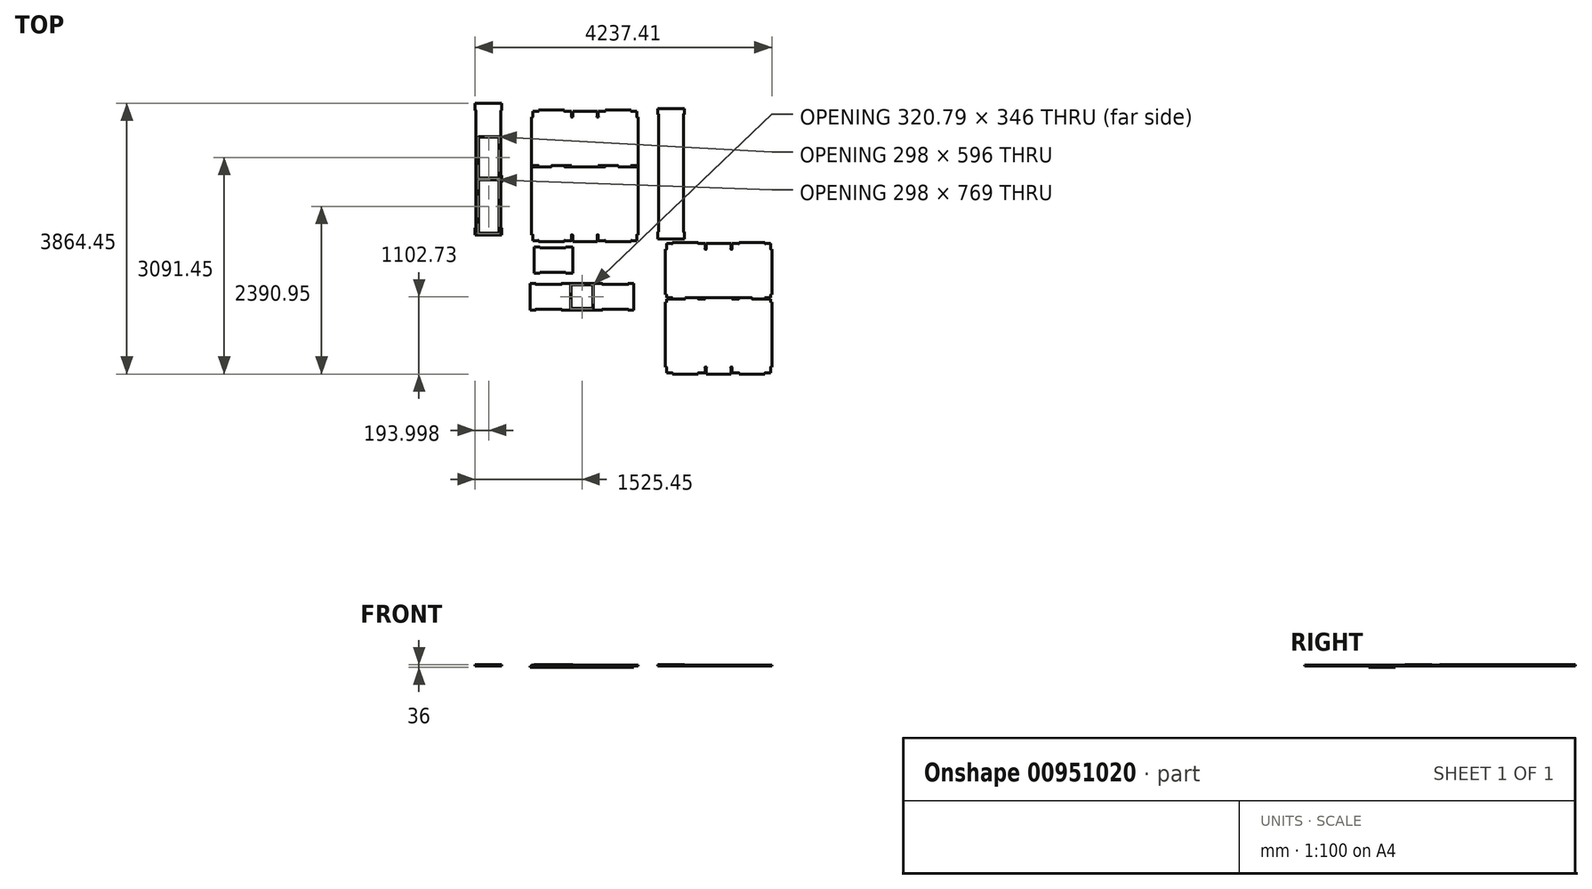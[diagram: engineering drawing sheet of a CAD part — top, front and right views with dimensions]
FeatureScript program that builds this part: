
annotation { "Feature Type Name" : "Feature", "Feature Type Description" : "" }
export const myFeature = defineFeature(function(context is Context, id is Id, definition is map)
    precondition{}
    {
        {
            assignVariable(context, id + "F0", {"name" : "thickness", "anyValue" : 18});
        }
        {
            assignVariable(context, id + "F1", {"name" : "Base", "anyValue" : 12});
        }
        {
            var Q0;
            Q0=qCreatedBy(makeId("Top.planeOp"),FACE);
            var sketch = newSketch(context, id + "F2", { "sketchPlane" : qUnion([Q0])});
            skLineSegment(sketch, "E0.bottom", {"start": v(-1460.53, 1782.83) * mm, "end": v(59.47, 1782.83) * mm});
            skLineSegment(sketch, "E0.top", {"start": v(-1460.53, -97.17) * mm, "end": v(59.47, -97.17) * mm});
            skLineSegment(sketch, "E0.left", {"start": v(-1460.53, 1782.83) * mm, "end": v(-1460.53, -97.17) * mm});
            skLineSegment(sketch, "E0.right", {"start": v(59.47, 1782.83) * mm, "end": v(59.47, -97.17) * mm});
            skLineSegment(sketch, "E1", {"start": v(-700.53, 1782.83) * mm, "end": v(-700.53, -97.17) * mm, "construction": true});
            skLineSegment(sketch, "E2.bottom", {"start": v(-875.53, 1782.83) * mm, "end": v(-893.53, 1782.83) * mm});
            skLineSegment(sketch, "E2.top", {"start": v(-875.53, 1682.83) * mm, "end": v(-893.53, 1682.83) * mm});
            skLineSegment(sketch, "E2.left", {"start": v(-875.53, 1782.83) * mm, "end": v(-875.53, 1682.83) * mm});
            skLineSegment(sketch, "E2.right", {"start": v(-893.53, 1782.83) * mm, "end": v(-893.53, 1682.83) * mm});
            skLineSegment(sketch, "E3.bottom", {"start": v(-875.53, -97.17) * mm, "end": v(-893.53, -97.17) * mm});
            skLineSegment(sketch, "E3.top", {"start": v(-875.53, 2.83) * mm, "end": v(-893.53, 2.83) * mm});
            skLineSegment(sketch, "E3.left", {"start": v(-875.53, -97.17) * mm, "end": v(-875.53, 2.83) * mm});
            skLineSegment(sketch, "E3.right", {"start": v(-893.53, -97.17) * mm, "end": v(-893.53, 2.83) * mm});
            skLineSegment(sketch, "E4.MirrorCS", {"start": v(-507.53, -97.17) * mm, "end": v(-507.53, 2.83) * mm});
            skLineSegment(sketch, "E5.MirrorCS", {"start": v(-525.53, -97.17) * mm, "end": v(-525.53, 2.83) * mm});
            skLineSegment(sketch, "E6.MirrorCS", {"start": v(-525.53, 2.83) * mm, "end": v(-507.53, 2.83) * mm});
            skLineSegment(sketch, "E7.MirrorCS", {"start": v(-525.53, -97.17) * mm, "end": v(-507.53, -97.17) * mm});
            skLineSegment(sketch, "E8.MirrorCS", {"start": v(-525.53, 1782.83) * mm, "end": v(-525.53, 1682.83) * mm});
            skLineSegment(sketch, "E9.MirrorCS", {"start": v(-525.53, 1682.83) * mm, "end": v(-507.53, 1682.83) * mm});
            skLineSegment(sketch, "E10.MirrorCS", {"start": v(-507.53, 1782.83) * mm, "end": v(-507.53, 1682.83) * mm});
            skLineSegment(sketch, "E11.MirrorCS", {"start": v(-525.53, 1782.83) * mm, "end": v(-507.53, 1782.83) * mm});
            skLineSegment(sketch, "E12.bottom", {"start": v(-1460.53, -97.17) * mm, "end": v(-1360.53, -97.17) * mm});
            skLineSegment(sketch, "E12.top", {"start": v(-1460.53, -79.17) * mm, "end": v(-1360.53, -79.17) * mm});
            skLineSegment(sketch, "E12.left", {"start": v(-1460.53, -97.17) * mm, "end": v(-1460.53, -79.17) * mm});
            skLineSegment(sketch, "E12.right", {"start": v(-1360.53, -97.17) * mm, "end": v(-1360.53, -79.17) * mm});
            skLineSegment(sketch, "E13.bottom", {"start": v(-893.53, -97.17) * mm, "end": v(-993.53, -97.17) * mm});
            skLineSegment(sketch, "E13.top", {"start": v(-893.53, -79.17) * mm, "end": v(-993.53, -79.17) * mm});
            skLineSegment(sketch, "E13.left", {"start": v(-893.53, -97.17) * mm, "end": v(-893.53, -79.17) * mm});
            skLineSegment(sketch, "E13.right", {"start": v(-993.53, -97.17) * mm, "end": v(-993.53, -79.17) * mm});
            skLineSegment(sketch, "E14.bottom", {"start": v(-893.53, 1782.83) * mm, "end": v(-993.53, 1782.83) * mm});
            skLineSegment(sketch, "E14.top", {"start": v(-893.53, 1764.83) * mm, "end": v(-993.53, 1764.83) * mm});
            skLineSegment(sketch, "E14.left", {"start": v(-893.53, 1782.83) * mm, "end": v(-893.53, 1764.83) * mm});
            skLineSegment(sketch, "E14.right", {"start": v(-993.53, 1782.83) * mm, "end": v(-993.53, 1764.83) * mm});
            skLineSegment(sketch, "E15.bottom", {"start": v(-1460.53, 1782.83) * mm, "end": v(-1360.53, 1782.83) * mm});
            skLineSegment(sketch, "E15.top", {"start": v(-1460.53, 1764.83) * mm, "end": v(-1360.53, 1764.83) * mm});
            skLineSegment(sketch, "E15.left", {"start": v(-1460.53, 1782.83) * mm, "end": v(-1460.53, 1764.83) * mm});
            skLineSegment(sketch, "E15.right", {"start": v(-1360.53, 1782.83) * mm, "end": v(-1360.53, 1764.83) * mm});
            skLineSegment(sketch, "E16.MirrorCS", {"start": v(-507.53, 1764.83) * mm, "end": v(-407.53, 1764.83) * mm});
            skLineSegment(sketch, "E17.MirrorCS", {"start": v(-407.53, 1782.83) * mm, "end": v(-407.53, 1764.83) * mm});
            skLineSegment(sketch, "E18.MirrorCS", {"start": v(59.47, 1764.83) * mm, "end": v(-40.53, 1764.83) * mm});
            skLineSegment(sketch, "E19.MirrorCS", {"start": v(-40.53, 1782.83) * mm, "end": v(-40.53, 1764.83) * mm});
            skLineSegment(sketch, "E20.MirrorCS", {"start": v(-507.53, -79.17) * mm, "end": v(-407.53, -79.17) * mm});
            skLineSegment(sketch, "E21.MirrorCS", {"start": v(-407.53, -97.17) * mm, "end": v(-407.53, -79.17) * mm});
            skLineSegment(sketch, "E22.MirrorCS", {"start": v(59.47, -79.17) * mm, "end": v(-40.53, -79.17) * mm});
            skLineSegment(sketch, "E23.MirrorCS", {"start": v(-40.53, -97.17) * mm, "end": v(-40.53, -79.17) * mm});
            skLineSegment(sketch, "E24.bottom", {"start": v(-1460.53, 1764.83) * mm, "end": v(-1442.53, 1764.83) * mm});
            skLineSegment(sketch, "E24.top", {"start": v(-1460.53, 1682.83) * mm, "end": v(-1442.53, 1682.83) * mm});
            skLineSegment(sketch, "E24.left", {"start": v(-1460.53, 1764.83) * mm, "end": v(-1460.53, 1682.83) * mm});
            skLineSegment(sketch, "E24.right", {"start": v(-1442.53, 1764.83) * mm, "end": v(-1442.53, 1682.83) * mm});
            skLineSegment(sketch, "E25.bottom", {"start": v(-1460.53, -79.17) * mm, "end": v(-1442.53, -79.17) * mm});
            skLineSegment(sketch, "E25.top", {"start": v(-1460.53, 2.83) * mm, "end": v(-1442.53, 2.83) * mm});
            skLineSegment(sketch, "E25.left", {"start": v(-1460.53, -79.17) * mm, "end": v(-1460.53, 2.83) * mm});
            skLineSegment(sketch, "E25.right", {"start": v(-1442.53, -79.17) * mm, "end": v(-1442.53, 2.83) * mm});
            skLineSegment(sketch, "E26.MirrorCS", {"start": v(59.47, 2.83) * mm, "end": v(41.47, 2.83) * mm});
            skLineSegment(sketch, "E27.MirrorCS", {"start": v(41.47, -79.17) * mm, "end": v(41.47, 2.83) * mm});
            skLineSegment(sketch, "E28.MirrorCS", {"start": v(59.47, 1682.83) * mm, "end": v(41.47, 1682.83) * mm});
            skLineSegment(sketch, "E29.MirrorCS", {"start": v(41.47, 1764.83) * mm, "end": v(41.47, 1682.83) * mm});
            skLineSegment(sketch, "E30", {"start": v(-1460.53, 982.83) * mm, "end": v(59.47, 982.83) * mm, "construction": true});
            skLineSegment(sketch, "E31", {"start": v(59.47, 982.83) * mm, "end": v(-930.26, 982.83) * mm, "construction": true});
            skLineSegment(sketch, "E32.bottom", {"start": v(-1460.53, 991.83) * mm, "end": v(-1360.53, 991.83) * mm});
            skLineSegment(sketch, "E32.top", {"start": v(-1442.53, 973.83) * mm, "end": v(-1360.53, 973.83) * mm});
            skLineSegment(sketch, "E32.left", {"start": v(-1460.53, 991.83) * mm, "end": v(-1460.53, 973.83) * mm});
            skLineSegment(sketch, "E32.right", {"start": v(-1360.53, 991.83) * mm, "end": v(-1360.53, 973.83) * mm});
            skLineSegment(sketch, "E33.bottom", {"start": v(-993.53, 991.83) * mm, "end": v(-893.53, 991.83) * mm});
            skLineSegment(sketch, "E33.top", {"start": v(-993.53, 973.83) * mm, "end": v(-893.53, 973.83) * mm});
            skLineSegment(sketch, "E33.left", {"start": v(-993.53, 991.83) * mm, "end": v(-993.53, 973.83) * mm});
            skLineSegment(sketch, "E33.right", {"start": v(-893.53, 991.83) * mm, "end": v(-893.53, 973.83) * mm});
            skLineSegment(sketch, "E34.MirrorCS", {"start": v(41.47, 973.83) * mm, "end": v(-40.53, 973.83) * mm});
            skLineSegment(sketch, "E35.MirrorCS", {"start": v(59.47, 991.83) * mm, "end": v(-40.53, 991.83) * mm});
            skLineSegment(sketch, "E36.MirrorCS", {"start": v(-40.53, 991.83) * mm, "end": v(-40.53, 973.83) * mm});
            skLineSegment(sketch, "E37.MirrorCS", {"start": v(-407.53, 973.83) * mm, "end": v(-507.53, 973.83) * mm});
            skLineSegment(sketch, "E38.MirrorCS", {"start": v(-407.53, 991.83) * mm, "end": v(-407.53, 973.83) * mm});
            skLineSegment(sketch, "E39.MirrorCS", {"start": v(-407.53, 991.83) * mm, "end": v(-507.53, 991.83) * mm});
            skLineSegment(sketch, "E40.MirrorCS", {"start": v(-507.53, 991.83) * mm, "end": v(-507.53, 973.83) * mm});
            skLineSegment(sketch, "E41.bottom", {"start": v(-1177.03, 991.83) * mm, "end": v(-993.53, 991.83) * mm});
            skLineSegment(sketch, "E41.top", {"start": v(-1360.53, 973.83) * mm, "end": v(-1177.03, 973.83) * mm});
            skLineSegment(sketch, "E42", {"start": v(-1177.03, 991.83) * mm, "end": v(-1177.03, 973.83) * mm});
            skLineSegment(sketch, "E43", {"start": v(-893.53, 973.83) * mm, "end": v(-507.53, 973.83) * mm});
            skLineSegment(sketch, "E44.bottom", {"start": v(-407.53, 991.83) * mm, "end": v(-224.03, 991.83) * mm});
            skLineSegment(sketch, "E44.top", {"start": v(-224.03, 973.83) * mm, "end": v(-40.53, 973.83) * mm});
            skLineSegment(sketch, "E45", {"start": v(-224.03, 991.83) * mm, "end": v(-224.03, 973.83) * mm});
            skLineSegment(sketch, "E46.bottom", {"start": v(-1460.53, 991.83) * mm, "end": v(-1442.53, 991.83) * mm});
            skLineSegment(sketch, "E46.left", {"start": v(-1460.53, 993.83) * mm, "end": v(-1460.53, 991.83) * mm});
            skLineSegment(sketch, "E46.right", {"start": v(-1442.53, 991.83) * mm, "end": v(-1442.53, 973.83) * mm});
            skLineSegment(sketch, "E47.bottom", {"start": v(59.47, 991.83) * mm, "end": v(41.47, 991.83) * mm});
            skLineSegment(sketch, "E47.left", {"start": v(59.47, 993.83) * mm, "end": v(59.47, 991.83) * mm});
            skLineSegment(sketch, "E47.right", {"start": v(41.47, 991.83) * mm, "end": v(41.47, 973.83) * mm});
            skPoint(sketch, "E48.orphan", {"position": v(59.47, 973.83) * mm});
            skLineSegment(sketch, "E49.bottom", {"start": v(-893.53, 1782.83) * mm, "end": v(-507.53, 1782.83) * mm});
            skLineSegment(sketch, "E49.top", {"start": v(-893.53, 1764.83) * mm, "end": v(-507.53, 1764.83) * mm});
            skLineSegment(sketch, "E49.right", {"start": v(-507.53, 1782.83) * mm, "end": v(-507.53, 1764.83) * mm});
            skCircle(sketch, "E50", {"center": v(-1445.35, 1685.66) * mm, "radius": 4 * mm});
            skLineSegment(sketch, "E51", {"start": v(-1442.53, 1682.83) * mm, "end": v(-1445.35, 1685.66) * mm});
            skCircle(sketch, "E52", {"center": v(-1363.15, 1767.84) * mm, "radius": 4 * mm});
            skLineSegment(sketch, "E53", {"start": v(-1360.53, 1764.83) * mm, "end": v(-1363.15, 1767.84) * mm});
            skCircle(sketch, "E54", {"center": v(-990.7, 1767.66) * mm, "radius": 4 * mm});
            skLineSegment(sketch, "E55", {"start": v(-993.53, 1764.83) * mm, "end": v(-990.7, 1767.66) * mm});
            skCircle(sketch, "E56", {"center": v(-890.7, 1685.66) * mm, "radius": 4 * mm});
            skLineSegment(sketch, "E57", {"start": v(-893.53, 1682.83) * mm, "end": v(-890.7, 1685.66) * mm});
            skCircle(sketch, "E58", {"center": v(-878.35, 1685.66) * mm, "radius": 4 * mm});
            skLineSegment(sketch, "E59", {"start": v(-875.53, 1682.83) * mm, "end": v(-878.35, 1685.66) * mm});
            skCircle(sketch, "E60", {"center": v(-1439.7, 976.66) * mm, "radius": 4 * mm});
            skCircle(sketch, "E61", {"center": v(-1363.35, 989) * mm, "radius": 4 * mm});
            skLineSegment(sketch, "E62", {"start": v(-1360.53, 991.83) * mm, "end": v(-1363.35, 989) * mm});
            skLineSegment(sketch, "E63", {"start": v(-1442.53, 973.83) * mm, "end": v(-1439.7, 976.66) * mm});
            skArc(sketch, "E64", {"start": v(-1171.37, 991.83) * mm, "mid": v(-1177.03, 991.83) * mm, "end": v(-1177.03, 986.17) * mm});
            skLineSegment(sketch, "E65", {"start": v(-1177.03, 991.83) * mm, "end": v(-1174.2, 989) * mm});
            skArc(sketch, "E66", {"start": v(-1182.68, 973.83) * mm, "mid": v(-1177.03, 973.83) * mm, "end": v(-1177.03, 979.49) * mm});
            skLineSegment(sketch, "E67", {"start": v(-1177.03, 973.83) * mm, "end": v(-1179.85, 976.66) * mm});
            skCircle(sketch, "E68", {"center": v(-990.7, 976.66) * mm, "radius": 4 * mm});
            skLineSegment(sketch, "E69", {"start": v(-993.53, 973.83) * mm, "end": v(-990.7, 976.66) * mm});
            skCircle(sketch, "E70", {"center": v(-896.35, 989) * mm, "radius": 4 * mm});
            skLineSegment(sketch, "E71", {"start": v(-893.53, 991.83) * mm, "end": v(-896.35, 989) * mm});
            skCircle(sketch, "E72", {"center": v(-1445.35, 0) * mm, "radius": 4 * mm});
            skLineSegment(sketch, "E73", {"start": v(-1442.53, 2.83) * mm, "end": v(-1445.35, 0) * mm});
            skCircle(sketch, "E74", {"center": v(-1363.35, -82) * mm, "radius": 4 * mm});
            skLineSegment(sketch, "E75", {"start": v(-1360.53, -79.17) * mm, "end": v(-1363.35, -82) * mm});
            skCircle(sketch, "E76", {"center": v(-990.7, -82) * mm, "radius": 4 * mm});
            skLineSegment(sketch, "E77", {"start": v(-993.53, -79.17) * mm, "end": v(-990.7, -82) * mm});
            skCircle(sketch, "E78", {"center": v(-890.7, 0) * mm, "radius": 4 * mm});
            skCircle(sketch, "E79", {"center": v(-878.35, 0) * mm, "radius": 4 * mm});
            skLineSegment(sketch, "E80", {"start": v(-875.53, 2.83) * mm, "end": v(-878.35, 0) * mm});
            skLineSegment(sketch, "E81", {"start": v(-893.53, 2.83) * mm, "end": v(-890.7, 0) * mm});
            skCircle(sketch, "E82.MirrorC", {"center": v(-522.7, 0) * mm, "radius": 4 * mm});
            skCircle(sketch, "E83.MirrorC", {"center": v(-510.35, 0) * mm, "radius": 4 * mm});
            skCircle(sketch, "E84.MirrorC", {"center": v(-410.35, -82) * mm, "radius": 4 * mm});
            skCircle(sketch, "E85.MirrorC", {"center": v(-37.7, -82) * mm, "radius": 4 * mm});
            skCircle(sketch, "E86.MirrorC", {"center": v(44.3, 0) * mm, "radius": 4 * mm});
            skCircle(sketch, "E87.MirrorC", {"center": v(38.65, 976.66) * mm, "radius": 4 * mm});
            skCircle(sketch, "E88.MirrorC", {"center": v(-37.7, 989) * mm, "radius": 4 * mm});
            skArc(sketch, "E89.MirrorCS", {"start": v(-218.37, 973.83) * mm, "mid": v(-224.03, 973.83) * mm, "end": v(-224.03, 979.49) * mm});
            skArc(sketch, "E90.MirrorCS", {"start": v(-229.68, 991.83) * mm, "mid": v(-224.03, 991.83) * mm, "end": v(-224.03, 986.17) * mm});
            skCircle(sketch, "E91.MirrorC", {"center": v(-410.35, 976.66) * mm, "radius": 4 * mm});
            skCircle(sketch, "E92.MirrorC", {"center": v(-504.7, 989) * mm, "radius": 4 * mm});
            skCircle(sketch, "E93.MirrorC", {"center": v(44.3, 1685.66) * mm, "radius": 4 * mm});
            skCircle(sketch, "E94.MirrorC", {"center": v(-37.9, 1767.84) * mm, "radius": 4 * mm});
            skCircle(sketch, "E95.MirrorC", {"center": v(-410.35, 1767.66) * mm, "radius": 4 * mm});
            skCircle(sketch, "E96.MirrorC", {"center": v(-510.35, 1685.66) * mm, "radius": 4 * mm});
            skCircle(sketch, "E97.MirrorC", {"center": v(-522.7, 1685.66) * mm, "radius": 4 * mm});
            skSolve(sketch);
        }
        {
            var Q0;
            {var subQ23=sQuery(id+"F2.wireOp",EDGE,"E43");Q0=makeQuery(id+"F2.imprint","IMPRINT",FACE,{"disambiguationData":[TD([[makeQuery(id+"F2.imprint","IMPRINT",EDGE,{"derivedFrom":subQ23}),1.0]])]});}
            extrude(context, id + "F3", {"entities" : qUnion([Q0]), "depth" : getVariable(context, 'Base') * mm, "offsetDistance" : 25 * mm});
        }
        {
            var Q0;
            Q0=qCreatedBy(makeId("Top.planeOp"),FACE);
            var sketch = newSketch(context, id + "F4", { "sketchPlane" : qUnion([Q0])});
            skLineSegment(sketch, "E98.bottom", {"start": v(719.43, 1805.64) * mm, "end": v(719.43, 1805.64) * mm});
            skLineSegment(sketch, "E98.top", {"start": v(719.43, -56.36) * mm, "end": v(719.43, -56.36) * mm});
            skLineSegment(sketch, "E98.left", {"start": v(719.43, 1805.64) * mm, "end": v(719.43, 1723.64) * mm});
            skLineSegment(sketch, "E98.right", {"start": v(719.43, 1805.64) * mm, "end": v(719.43, -56.36) * mm});
            skLineSegment(sketch, "E99.bottom", {"start": v(719.43, 1805.64) * mm, "end": v(339.43, 1805.64) * mm});
            skLineSegment(sketch, "E99.top", {"start": v(719.43, -56.36) * mm, "end": v(339.43, -56.36) * mm});
            skLineSegment(sketch, "E99.right", {"start": v(339.43, 1805.64) * mm, "end": v(339.43, -56.36) * mm});
            skLineSegment(sketch, "E100.bottom", {"start": v(339.43, 1805.64) * mm, "end": v(719.43, 1805.64) * mm});
            skLineSegment(sketch, "E100.top", {"start": v(339.43, 1723.64) * mm, "end": v(719.43, 1723.64) * mm});
            skLineSegment(sketch, "E100.right", {"start": v(339.43, 1805.64) * mm, "end": v(339.43, 1723.64) * mm});
            skLineSegment(sketch, "E101.top", {"start": v(719.43, 43.64) * mm, "end": v(339.43, 43.64) * mm});
            skLineSegment(sketch, "E101.left", {"start": v(339.43, -56.36) * mm, "end": v(339.43, 43.64) * mm});
            skLineSegment(sketch, "E101.right", {"start": v(719.43, -56.36) * mm, "end": v(719.43, 43.64) * mm});
            skLineSegment(sketch, "E102.trimOffspring", {"start": v(719.43, 43.64) * mm, "end": v(719.43, -56.36) * mm});
            skLineSegment(sketch, "E103.bottom", {"start": v(719.43, 1723.64) * mm, "end": v(707.43, 1723.64) * mm});
            skLineSegment(sketch, "E103.top", {"start": v(719.43, 43.64) * mm, "end": v(707.43, 43.64) * mm});
            skLineSegment(sketch, "E103.left", {"start": v(719.43, 1723.64) * mm, "end": v(719.43, 43.64) * mm});
            skLineSegment(sketch, "E103.right", {"start": v(707.43, 1723.64) * mm, "end": v(707.43, 43.64) * mm});
            skLineSegment(sketch, "E104.bottom", {"start": v(339.43, 43.64) * mm, "end": v(352.43, 43.64) * mm});
            skLineSegment(sketch, "E104.top", {"start": v(339.43, 1723.64) * mm, "end": v(352.43, 1723.64) * mm});
            skLineSegment(sketch, "E104.left", {"start": v(339.43, 43.64) * mm, "end": v(339.43, 1723.64) * mm});
            skLineSegment(sketch, "E104.right", {"start": v(352.43, 43.64) * mm, "end": v(352.43, 1723.64) * mm});
            skCircle(sketch, "E105", {"center": v(349.6, 46.47) * mm, "radius": 4 * mm});
            skLineSegment(sketch, "E106", {"start": v(352.43, 43.64) * mm, "end": v(349.6, 46.47) * mm});
            skCircle(sketch, "E107", {"center": v(710.26, 46.47) * mm, "radius": 4 * mm});
            skLineSegment(sketch, "E108", {"start": v(707.43, 43.64) * mm, "end": v(710.26, 46.47) * mm});
            skCircle(sketch, "E109", {"center": v(349.6, 1720.82) * mm, "radius": 4 * mm});
            skLineSegment(sketch, "E110", {"start": v(352.43, 1723.64) * mm, "end": v(349.6, 1720.82) * mm});
            skCircle(sketch, "E111", {"center": v(710.26, 1720.82) * mm, "radius": 4 * mm});
            skLineSegment(sketch, "E112", {"start": v(707.43, 1723.64) * mm, "end": v(710.26, 1720.82) * mm});
            skSolve(sketch);
        }
        {
            var Q0;
            {var subQ9=sQuery(id+"F4.wireOp",EDGE,"E98.left");Q0=makeQuery(id+"F4.imprint","IMPRINT",FACE,{"disambiguationData":[TD([[makeQuery(id+"F4.imprint","IMPRINT",EDGE,{"derivedFrom":subQ9}),-1.0]])]});}
            var Q1;
            {var subQ7=sQuery(id+"F4.wireOp",EDGE,"E111");var subQ8=sQuery(id+"F4.wireOp",EDGE,"E103.right");var subQ9=makeQuery(id+"F4.imprint","INTERSECT",VERTEX,{"derivedFrom":[subQ8,subQ7]});Q1=makeQuery(id+"F4.imprint","IMPRINT",FACE,{"disambiguationData":[TD([[makeQuery(id+"F4.imprint","IMPRINT",EDGE,{"disambiguationData":[TD([[subQ9,-1.0]])],"derivedFrom":subQ8}),-1.0]])]});}
            var Q2;
            {var subQ5=sQuery(id+"F4.wireOp",EDGE,"E99.top");Q2=makeQuery(id+"F4.imprint","IMPRINT",FACE,{"disambiguationData":[TD([[makeQuery(id+"F4.imprint","IMPRINT",EDGE,{"derivedFrom":subQ5}),-1.0]])]});}
            extrude(context, id + "F5", {"entities" : qUnion([Q0, Q1, Q2]), "depth" : (getVariable(context, 'thickness')) * mm, "offsetDistance" : 25 * mm});
        }
        {
            var Q0;
            Q0=qCreatedBy(makeId("Top.planeOp"),FACE);
            var sketch = newSketch(context, id + "F6", { "sketchPlane" : qUnion([Q0])});
            skLineSegment(sketch, "E113.bottom", {"start": v(-1440.4, -167.9) * mm, "end": v(-873.9, -167.9) * mm});
            skLineSegment(sketch, "E113.top", {"start": v(-1440.4, -547.9) * mm, "end": v(-873.9, -547.9) * mm});
            skLineSegment(sketch, "E113.left", {"start": v(-1440.4, -167.9) * mm, "end": v(-1440.4, -547.9) * mm});
            skLineSegment(sketch, "E113.right", {"start": v(-873.9, -167.9) * mm, "end": v(-873.9, -547.9) * mm});
            skLineSegment(sketch, "E114.bottom", {"start": v(-873.9, -547.9) * mm, "end": v(-1440.4, -547.9) * mm});
            skLineSegment(sketch, "E114.top", {"start": v(-973.9, -180.9) * mm, "end": v(-1340.4, -180.9) * mm});
            skLineSegment(sketch, "E114.left", {"start": v(-873.9, -547.9) * mm, "end": v(-873.9, -180.9) * mm});
            skLineSegment(sketch, "E114.right", {"start": v(-1440.4, -547.9) * mm, "end": v(-1440.4, -180.9) * mm});
            skLineSegment(sketch, "E115.bottom", {"start": v(-1340.4, -167.9) * mm, "end": v(-973.9, -167.9) * mm});
            skLineSegment(sketch, "E115.top", {"start": v(-1340.4, -180.9) * mm, "end": v(-973.9, -180.9) * mm});
            skLineSegment(sketch, "E115.left", {"start": v(-1340.4, -167.9) * mm, "end": v(-1340.4, -180.9) * mm});
            skLineSegment(sketch, "E115.right", {"start": v(-973.9, -167.9) * mm, "end": v(-973.9, -180.9) * mm});
            skLineSegment(sketch, "E116.bottom", {"start": v(-1340.4, -547.9) * mm, "end": v(-973.9, -547.9) * mm});
            skLineSegment(sketch, "E116.top", {"start": v(-1340.4, -535.9) * mm, "end": v(-973.9, -535.9) * mm});
            skLineSegment(sketch, "E116.left", {"start": v(-1340.4, -547.9) * mm, "end": v(-1340.4, -535.9) * mm});
            skLineSegment(sketch, "E116.right", {"start": v(-973.9, -547.9) * mm, "end": v(-973.9, -535.9) * mm});
            skLineSegment(sketch, "E117.bottom", {"start": v(-1440.4, -167.9) * mm, "end": v(-1422.4, -167.9) * mm});
            skLineSegment(sketch, "E117.top", {"start": v(-1440.4, -547.9) * mm, "end": v(-1422.4, -547.9) * mm});
            skLineSegment(sketch, "E117.right", {"start": v(-1422.4, -167.9) * mm, "end": v(-1422.4, -547.9) * mm});
            skLineSegment(sketch, "E118.trimOffspring", {"start": v(-1422.4, -180.9) * mm, "end": v(-1440.4, -180.9) * mm});
            skCircle(sketch, "E119", {"center": v(-1337.57, -178.07) * mm, "radius": 4 * mm});
            skLineSegment(sketch, "E120", {"start": v(-1340.4, -180.9) * mm, "end": v(-1337.57, -178.07) * mm});
            skCircle(sketch, "E121", {"center": v(-976.72, -178.07) * mm, "radius": 4 * mm});
            skLineSegment(sketch, "E122", {"start": v(-973.9, -180.9) * mm, "end": v(-976.72, -178.07) * mm});
            skCircle(sketch, "E123", {"center": v(-1337.57, -538.73) * mm, "radius": 4 * mm});
            skLineSegment(sketch, "E124", {"start": v(-1340.4, -535.9) * mm, "end": v(-1337.57, -538.73) * mm});
            skCircle(sketch, "E125", {"center": v(-976.72, -538.73) * mm, "radius": 4 * mm});
            skLineSegment(sketch, "E126", {"start": v(-973.9, -535.9) * mm, "end": v(-976.72, -538.73) * mm});
            skSolve(sketch);
        }
        {
            var Q0;
            {var subQ12=sQuery(id+"F6.wireOp",EDGE,"E113.right");var subQ13=makeQuery(id+"F6.imprint","IMPRINT",VERTEX,{"derivedFrom":subQ12});Q0=makeQuery(id+"F6.imprint","IMPRINT",FACE,{"disambiguationData":[TD([[makeQuery(id+"F6.imprint","IMPRINT",EDGE,{"disambiguationData":[TD([[subQ13,-1.0]])],"derivedFrom":subQ12}),-1.0]])]});}
            extrude(context, id + "F7", {"entities" : qUnion([Q0]), "depth" : (getVariable(context, 'thickness')) * mm, "offsetDistance" : 25 * mm});
        }
        {
            var Q0;
            Q0=qCreatedBy(makeId("Top.planeOp"),FACE);
            var sketch = newSketch(context, id + "F8", { "sketchPlane" : qUnion([Q0])});
            skLineSegment(sketch, "E127.bottom", {"start": v(-1887.45, 1880) * mm, "end": v(-2267.45, 1880) * mm});
            skLineSegment(sketch, "E127.top", {"start": v(-1887.45, 0) * mm, "end": v(-2267.45, 0) * mm});
            skLineSegment(sketch, "E127.right", {"start": v(-2267.45, 1880) * mm, "end": v(-2267.45, 0) * mm});
            skLineSegment(sketch, "E128", {"start": v(-2179.45, 1480) * mm, "end": v(-1916.45, 1480) * mm, "construction": true});
            skLineSegment(sketch, "E129", {"start": v(-2179.45, 800) * mm, "end": v(-1916.45, 800) * mm, "construction": true});
            skLineSegment(sketch, "E130.bottom", {"start": v(-2212.45, 1405) * mm, "end": v(-1934.45, 1405) * mm});
            skLineSegment(sketch, "E130.top", {"start": v(-2212.45, 809) * mm, "end": v(-1934.45, 809) * mm});
            skLineSegment(sketch, "E130.left", {"start": v(-2222.45, 1395) * mm, "end": v(-2222.45, 819) * mm});
            skLineSegment(sketch, "E130.right", {"start": v(-1924.45, 1395) * mm, "end": v(-1924.45, 819) * mm});
            skLineSegment(sketch, "E131.top", {"start": v(-2212.45, 791) * mm, "end": v(-1934.45, 791) * mm});
            skLineSegment(sketch, "E131.left", {"start": v(-2222.45, 32) * mm, "end": v(-2222.45, 781) * mm});
            skLineSegment(sketch, "E131.right", {"start": v(-1924.45, 32) * mm, "end": v(-1924.45, 781) * mm});
            skPoint(sketch, "E132.visualSharp", {"position": v(-2222.45, 809) * mm});
            skPoint(sketch, "E133.visualSharp", {"position": v(-1924.45, 809) * mm});
            skPoint(sketch, "E134.visualSharp", {"position": v(-1924.45, 1405) * mm});
            skPoint(sketch, "E135.visualSharp", {"position": v(-2222.45, 1405) * mm});
            skPoint(sketch, "E136.visualSharp", {"position": v(-2222.45, 791) * mm});
            skPoint(sketch, "E137.visualSharp", {"position": v(-1924.45, 791) * mm});
            skPoint(sketch, "E138.visualSharp", {"position": v(-2222.45, 22) * mm});
            skPoint(sketch, "E139.visualSharp", {"position": v(-1924.45, 22) * mm});
            skLineSegment(sketch, "E140.bottom", {"start": v(-2267.45, 1780) * mm, "end": v(-2255.45, 1780) * mm});
            skLineSegment(sketch, "E140.top", {"start": v(-2267.45, 100) * mm, "end": v(-2255.45, 100) * mm});
            skLineSegment(sketch, "E140.left", {"start": v(-2267.45, 1780) * mm, "end": v(-2267.45, 100) * mm});
            skLineSegment(sketch, "E140.right", {"start": v(-2255.45, 1780) * mm, "end": v(-2255.45, 100) * mm});
            skLineSegment(sketch, "E141", {"start": v(-2212.45, 22) * mm, "end": v(-1934.45, 22) * mm});
            skLineSegment(sketch, "E142", {"start": v(-1887.45, 0) * mm, "end": v(-1887.45, 1880) * mm});
            skLineSegment(sketch, "E143.bottom", {"start": v(-1887.45, 0) * mm, "end": v(-1900.45, 0) * mm});
            skLineSegment(sketch, "E143.top", {"start": v(-1887.45, 100) * mm, "end": v(-1900.45, 100) * mm});
            skLineSegment(sketch, "E143.left", {"start": v(-1887.45, 0) * mm, "end": v(-1887.45, 100) * mm});
            skLineSegment(sketch, "E143.right", {"start": v(-1900.45, 0) * mm, "end": v(-1900.45, 100) * mm});
            skLineSegment(sketch, "E144.bottom", {"start": v(-1887.45, 1880) * mm, "end": v(-1900.45, 1880) * mm});
            skLineSegment(sketch, "E144.top", {"start": v(-1887.45, 1780) * mm, "end": v(-1900.45, 1780) * mm});
            skLineSegment(sketch, "E144.left", {"start": v(-1887.45, 1880) * mm, "end": v(-1887.45, 1780) * mm});
            skLineSegment(sketch, "E144.right", {"start": v(-1900.45, 1880) * mm, "end": v(-1900.45, 1780) * mm});
            skLineSegment(sketch, "E145.bottom", {"start": v(-1887.45, 750) * mm, "end": v(-1900.45, 750) * mm});
            skLineSegment(sketch, "E145.top", {"start": v(-1887.45, 850) * mm, "end": v(-1900.45, 850) * mm});
            skLineSegment(sketch, "E145.left", {"start": v(-1887.45, 750) * mm, "end": v(-1887.45, 850) * mm});
            skLineSegment(sketch, "E145.right", {"start": v(-1900.45, 750) * mm, "end": v(-1900.45, 850) * mm});
            skLineSegment(sketch, "E146", {"start": v(-1900.45, 100) * mm, "end": v(-1900.45, 750) * mm});
            skLineSegment(sketch, "E147", {"start": v(-1900.45, 850) * mm, "end": v(-1900.45, 1780) * mm});
            skLineSegment(sketch, "E148.1", {"start": v(-2212.45, 27) * mm, "end": v(-1934.45, 27) * mm});
            skLineSegment(sketch, "E148.2", {"start": v(-2217.45, 32) * mm, "end": v(-2217.45, 781) * mm});
            skLineSegment(sketch, "E148.5", {"start": v(-2212.45, 786) * mm, "end": v(-1934.45, 786) * mm});
            skLineSegment(sketch, "E148.7", {"start": v(-1929.45, 32) * mm, "end": v(-1929.45, 781) * mm});
            skLineSegment(sketch, "E149.1", {"start": v(-2212.45, 1400) * mm, "end": v(-1934.45, 1400) * mm});
            skLineSegment(sketch, "E149.2", {"start": v(-2217.45, 1395) * mm, "end": v(-2217.45, 819) * mm});
            skLineSegment(sketch, "E149.5", {"start": v(-2212.45, 814) * mm, "end": v(-1934.45, 814) * mm});
            skLineSegment(sketch, "E149.7", {"start": v(-1929.45, 1395) * mm, "end": v(-1929.45, 819) * mm});
            skPoint(sketch, "E150.visualSharp", {"position": v(-1929.45, 27) * mm});
            skArc(sketch, "E151.filletArc", {"start": v(-1934.45, 22) * mm, "mid": v(-1927.38, 24.93) * mm, "end": v(-1924.45, 32) * mm});
            skArc(sketch, "E152.0", {"start": v(-1934.45, 27) * mm, "mid": v(-1930.92, 28.46) * mm, "end": v(-1929.45, 32) * mm});
            skPoint(sketch, "E153.visualSharp", {"position": v(-1929.45, 786) * mm});
            skArc(sketch, "E153.filletArc", {"start": v(-1929.45, 781) * mm, "mid": v(-1930.92, 784.54) * mm, "end": v(-1934.45, 786) * mm});
            skArc(sketch, "E154.filletArc", {"start": v(-1924.45, 781) * mm, "mid": v(-1927.38, 788.07) * mm, "end": v(-1934.45, 791) * mm});
            skArc(sketch, "E155.filletArc", {"start": v(-1934.45, 809) * mm, "mid": v(-1927.38, 811.93) * mm, "end": v(-1924.45, 819) * mm});
            skPoint(sketch, "E156.visualSharp", {"position": v(-1929.45, 814) * mm});
            skArc(sketch, "E156.filletArc", {"start": v(-1934.45, 814) * mm, "mid": v(-1930.92, 815.46) * mm, "end": v(-1929.45, 819) * mm});
            skPoint(sketch, "E157.visualSharp", {"position": v(-1929.45, 1400) * mm});
            skArc(sketch, "E157.filletArc", {"start": v(-1929.45, 1395) * mm, "mid": v(-1930.92, 1398.54) * mm, "end": v(-1934.45, 1400) * mm});
            skArc(sketch, "E158.filletArc", {"start": v(-1924.45, 1395) * mm, "mid": v(-1927.38, 1402.07) * mm, "end": v(-1934.45, 1405) * mm});
            skPoint(sketch, "E159.visualSharp", {"position": v(-2217.45, 1400) * mm});
            skArc(sketch, "E159.filletArc", {"start": v(-2212.45, 1400) * mm, "mid": v(-2215.99, 1398.54) * mm, "end": v(-2217.45, 1395) * mm});
            skArc(sketch, "E160.filletArc", {"start": v(-2212.45, 1405) * mm, "mid": v(-2219.52, 1402.07) * mm, "end": v(-2222.45, 1395) * mm});
            skArc(sketch, "E161.filletArc", {"start": v(-2222.45, 819) * mm, "mid": v(-2219.52, 811.93) * mm, "end": v(-2212.45, 809) * mm});
            skPoint(sketch, "E162.visualSharp", {"position": v(-2217.45, 814) * mm});
            skArc(sketch, "E162.filletArc", {"start": v(-2217.45, 819) * mm, "mid": v(-2215.99, 815.46) * mm, "end": v(-2212.45, 814) * mm});
            skPoint(sketch, "E163.visualSharp", {"position": v(-2217.45, 27) * mm});
            skArc(sketch, "E163.filletArc", {"start": v(-2217.45, 32) * mm, "mid": v(-2215.99, 28.46) * mm, "end": v(-2212.45, 27) * mm});
            skArc(sketch, "E164.filletArc", {"start": v(-2222.45, 32) * mm, "mid": v(-2219.52, 24.93) * mm, "end": v(-2212.45, 22) * mm});
            skPoint(sketch, "E165.visualSharp", {"position": v(-2217.45, 786) * mm});
            skArc(sketch, "E165.filletArc", {"start": v(-2212.45, 786) * mm, "mid": v(-2215.99, 784.54) * mm, "end": v(-2217.45, 781) * mm});
            skArc(sketch, "E166.filletArc", {"start": v(-2212.45, 791) * mm, "mid": v(-2219.52, 788.07) * mm, "end": v(-2222.45, 781) * mm});
            skCircle(sketch, "E167", {"center": v(-2258.28, 1777.17) * mm, "radius": 4 * mm});
            skLineSegment(sketch, "E168", {"start": v(-2255.45, 1780) * mm, "end": v(-2258.28, 1777.17) * mm});
            skCircle(sketch, "E169", {"center": v(-2258.28, 102.83) * mm, "radius": 4 * mm});
            skLineSegment(sketch, "E170", {"start": v(-2255.45, 100) * mm, "end": v(-2258.28, 102.83) * mm});
            skCircle(sketch, "E171", {"center": v(-1897.62, 102.83) * mm, "radius": 4 * mm});
            skLineSegment(sketch, "E172", {"start": v(-1900.45, 100) * mm, "end": v(-1897.62, 102.83) * mm});
            skCircle(sketch, "E173", {"center": v(-1897.62, 747.17) * mm, "radius": 4 * mm});
            skLineSegment(sketch, "E174", {"start": v(-1900.45, 750) * mm, "end": v(-1897.62, 747.17) * mm});
            skCircle(sketch, "E175.MirrorC", {"center": v(-1897.62, 852.83) * mm, "radius": 4 * mm});
            skCircle(sketch, "E176", {"center": v(-1897.62, 1777.17) * mm, "radius": 4 * mm});
            skLineSegment(sketch, "E177", {"start": v(-1900.45, 1780) * mm, "end": v(-1897.62, 1777.17) * mm});
            skSolve(sketch);
        }
        {
            var Q0;
            Q0=makeQuery(id+"F8.imprint","IMPRINT",FACE,{"disambiguationData":[TD([[makeQuery(id+"F8.imprint","IMPRINT",EDGE,{"derivedFrom":sQuery(id+"F8.wireOp",EDGE,"E130.bottom")}),1.0]])]});
            var Q1;
            Q1=makeQuery(id+"F8.imprint","IMPRINT",FACE,{"disambiguationData":[TD([[makeQuery(id+"F8.imprint","IMPRINT",EDGE,{"derivedFrom":sQuery(id+"F8.wireOp",EDGE,"E149.1")}),-1.0]])]});
            var Q2;
            Q2=makeQuery(id+"F8.imprint","IMPRINT",FACE,{"disambiguationData":[TD([[makeQuery(id+"F8.imprint","IMPRINT",EDGE,{"derivedFrom":sQuery(id+"F8.wireOp",EDGE,"E148.1")}),1.0]])]});
            var Q3;
            {var subQ0=sQuery(id+"F8.wireOp",EDGE,"E144.right");Q3=makeQuery(id+"F8.imprint","IMPRINT",FACE,{"disambiguationData":[TD([[makeQuery(id+"F8.imprint","IMPRINT",EDGE,{"derivedFrom":subQ0}),1.0]])]});}
            var Q4;
            {var subQ0=sQuery(id+"F8.wireOp",EDGE,"E145.right");Q4=makeQuery(id+"F8.imprint","IMPRINT",FACE,{"disambiguationData":[TD([[makeQuery(id+"F8.imprint","IMPRINT",EDGE,{"derivedFrom":subQ0}),-1.0]])]});}
            var Q5;
            {var subQ0=sQuery(id+"F8.wireOp",EDGE,"E143.right");Q5=makeQuery(id+"F8.imprint","IMPRINT",FACE,{"disambiguationData":[TD([[makeQuery(id+"F8.imprint","IMPRINT",EDGE,{"derivedFrom":subQ0}),-1.0]])]});}
            extrude(context, id + "F9", {"entities" : qUnion([Q0, Q1, Q2, Q3, Q4, Q5]), "depth" : (getVariable(context, 'thickness')) * mm, "offsetDistance" : 25 * mm});
        }
        {
            var Q0;
            Q0=qCreatedBy(makeId("Top.planeOp"),FACE);
            var sketch = newSketch(context, id + "F10", { "sketchPlane" : qUnion([Q0])});
            skLineSegment(sketch, "E178.bottom", {"start": v(449.96, -104.45) * mm, "end": v(1969.96, -104.45) * mm});
            skLineSegment(sketch, "E178.top", {"start": v(449.96, -1984.45) * mm, "end": v(1969.96, -1984.45) * mm});
            skLineSegment(sketch, "E178.left", {"start": v(449.96, -104.45) * mm, "end": v(449.96, -1984.45) * mm});
            skLineSegment(sketch, "E178.right", {"start": v(1969.96, -104.45) * mm, "end": v(1969.96, -1984.45) * mm});
            skLineSegment(sketch, "E179", {"start": v(1209.96, -104.45) * mm, "end": v(1209.96, -1984.45) * mm, "construction": true});
            skLineSegment(sketch, "E180.bottom", {"start": v(1034.96, -104.45) * mm, "end": v(1016.96, -104.45) * mm});
            skLineSegment(sketch, "E180.top", {"start": v(1034.96, -204.45) * mm, "end": v(1016.96, -204.45) * mm});
            skLineSegment(sketch, "E180.left", {"start": v(1034.96, -104.45) * mm, "end": v(1034.96, -204.45) * mm});
            skLineSegment(sketch, "E180.right", {"start": v(1016.96, -104.45) * mm, "end": v(1016.96, -204.45) * mm});
            skLineSegment(sketch, "E181.bottom", {"start": v(1034.96, -1984.45) * mm, "end": v(1016.96, -1984.45) * mm});
            skLineSegment(sketch, "E181.top", {"start": v(1034.96, -1884.45) * mm, "end": v(1016.96, -1884.45) * mm});
            skLineSegment(sketch, "E181.left", {"start": v(1034.96, -1984.45) * mm, "end": v(1034.96, -1884.45) * mm});
            skLineSegment(sketch, "E181.right", {"start": v(1016.96, -1984.45) * mm, "end": v(1016.96, -1884.45) * mm});
            skLineSegment(sketch, "E182.MirrorCS", {"start": v(1402.96, -1984.45) * mm, "end": v(1402.96, -1884.45) * mm});
            skLineSegment(sketch, "E183.MirrorCS", {"start": v(1384.96, -1984.45) * mm, "end": v(1384.96, -1884.45) * mm});
            skLineSegment(sketch, "E184.MirrorCS", {"start": v(1384.96, -1884.45) * mm, "end": v(1402.96, -1884.45) * mm});
            skLineSegment(sketch, "E185.MirrorCS", {"start": v(1384.96, -1984.45) * mm, "end": v(1402.96, -1984.45) * mm});
            skLineSegment(sketch, "E186.MirrorCS", {"start": v(1384.96, -104.45) * mm, "end": v(1384.96, -204.45) * mm});
            skLineSegment(sketch, "E187.MirrorCS", {"start": v(1384.96, -204.45) * mm, "end": v(1402.96, -204.45) * mm});
            skLineSegment(sketch, "E188.MirrorCS", {"start": v(1402.96, -104.45) * mm, "end": v(1402.96, -204.45) * mm});
            skLineSegment(sketch, "E189.MirrorCS", {"start": v(1384.96, -104.45) * mm, "end": v(1402.96, -104.45) * mm});
            skLineSegment(sketch, "E190.bottom", {"start": v(449.96, -1984.45) * mm, "end": v(549.96, -1984.45) * mm});
            skLineSegment(sketch, "E190.top", {"start": v(449.96, -1966.45) * mm, "end": v(549.96, -1966.45) * mm});
            skLineSegment(sketch, "E190.left", {"start": v(449.96, -1984.45) * mm, "end": v(449.96, -1966.45) * mm});
            skLineSegment(sketch, "E190.right", {"start": v(549.96, -1984.45) * mm, "end": v(549.96, -1966.45) * mm});
            skLineSegment(sketch, "E191.bottom", {"start": v(1016.96, -1984.45) * mm, "end": v(916.96, -1984.45) * mm});
            skLineSegment(sketch, "E191.top", {"start": v(1016.96, -1966.45) * mm, "end": v(916.96, -1966.45) * mm});
            skLineSegment(sketch, "E191.left", {"start": v(1016.96, -1984.45) * mm, "end": v(1016.96, -1966.45) * mm});
            skLineSegment(sketch, "E191.right", {"start": v(916.96, -1984.45) * mm, "end": v(916.96, -1966.45) * mm});
            skLineSegment(sketch, "E192.bottom", {"start": v(1016.96, -104.45) * mm, "end": v(916.96, -104.45) * mm});
            skLineSegment(sketch, "E192.top", {"start": v(1016.96, -122.45) * mm, "end": v(916.96, -122.45) * mm});
            skLineSegment(sketch, "E192.left", {"start": v(1016.96, -104.45) * mm, "end": v(1016.96, -122.45) * mm});
            skLineSegment(sketch, "E192.right", {"start": v(916.96, -104.45) * mm, "end": v(916.96, -122.45) * mm});
            skLineSegment(sketch, "E193.bottom", {"start": v(449.96, -104.45) * mm, "end": v(549.96, -104.45) * mm});
            skLineSegment(sketch, "E193.top", {"start": v(449.96, -122.45) * mm, "end": v(549.96, -122.45) * mm});
            skLineSegment(sketch, "E193.left", {"start": v(449.96, -104.45) * mm, "end": v(449.96, -122.45) * mm});
            skLineSegment(sketch, "E193.right", {"start": v(549.96, -104.45) * mm, "end": v(549.96, -122.45) * mm});
            skLineSegment(sketch, "E194.MirrorCS", {"start": v(1402.96, -122.45) * mm, "end": v(1502.96, -122.45) * mm});
            skLineSegment(sketch, "E195.MirrorCS", {"start": v(1502.96, -104.45) * mm, "end": v(1502.96, -122.45) * mm});
            skLineSegment(sketch, "E196.MirrorCS", {"start": v(1969.96, -122.45) * mm, "end": v(1869.96, -122.45) * mm});
            skLineSegment(sketch, "E197.MirrorCS", {"start": v(1869.96, -104.45) * mm, "end": v(1869.96, -122.45) * mm});
            skLineSegment(sketch, "E198.MirrorCS", {"start": v(1402.96, -1966.45) * mm, "end": v(1502.96, -1966.45) * mm});
            skLineSegment(sketch, "E199.MirrorCS", {"start": v(1502.96, -1984.45) * mm, "end": v(1502.96, -1966.45) * mm});
            skLineSegment(sketch, "E200.MirrorCS", {"start": v(1969.96, -1966.45) * mm, "end": v(1869.96, -1966.45) * mm});
            skLineSegment(sketch, "E201.MirrorCS", {"start": v(1869.96, -1984.45) * mm, "end": v(1869.96, -1966.45) * mm});
            skLineSegment(sketch, "E202.bottom", {"start": v(449.96, -122.45) * mm, "end": v(467.96, -122.45) * mm});
            skLineSegment(sketch, "E202.top", {"start": v(449.96, -204.45) * mm, "end": v(467.96, -204.45) * mm});
            skLineSegment(sketch, "E202.left", {"start": v(449.96, -122.45) * mm, "end": v(449.96, -204.45) * mm});
            skLineSegment(sketch, "E202.right", {"start": v(467.96, -122.45) * mm, "end": v(467.96, -204.45) * mm});
            skLineSegment(sketch, "E203.bottom", {"start": v(449.96, -1966.45) * mm, "end": v(467.96, -1966.45) * mm});
            skLineSegment(sketch, "E203.top", {"start": v(449.96, -1884.45) * mm, "end": v(467.96, -1884.45) * mm});
            skLineSegment(sketch, "E203.left", {"start": v(449.96, -1966.45) * mm, "end": v(449.96, -1884.45) * mm});
            skLineSegment(sketch, "E203.right", {"start": v(467.96, -1966.45) * mm, "end": v(467.96, -1884.45) * mm});
            skLineSegment(sketch, "E204.MirrorCS", {"start": v(1969.96, -1884.45) * mm, "end": v(1951.96, -1884.45) * mm});
            skLineSegment(sketch, "E205.MirrorCS", {"start": v(1951.96, -1966.45) * mm, "end": v(1951.96, -1884.45) * mm});
            skLineSegment(sketch, "E206.MirrorCS", {"start": v(1969.96, -204.45) * mm, "end": v(1951.96, -204.45) * mm});
            skLineSegment(sketch, "E207.MirrorCS", {"start": v(1951.96, -122.45) * mm, "end": v(1951.96, -204.45) * mm});
            skLineSegment(sketch, "E208", {"start": v(449.96, -904.45) * mm, "end": v(1969.96, -904.45) * mm, "construction": true});
            skLineSegment(sketch, "E209", {"start": v(1969.96, -904.45) * mm, "end": v(296.6, -904.45) * mm, "construction": true});
            skLineSegment(sketch, "E210.bottom", {"start": v(449.96, -895.45) * mm, "end": v(549.96, -895.45) * mm});
            skLineSegment(sketch, "E210.top", {"start": v(449.96, -913.45) * mm, "end": v(549.96, -913.45) * mm});
            skLineSegment(sketch, "E210.left", {"start": v(449.96, -895.45) * mm, "end": v(449.96, -913.45) * mm});
            skLineSegment(sketch, "E210.right", {"start": v(549.96, -895.45) * mm, "end": v(549.96, -913.45) * mm});
            skLineSegment(sketch, "E211.bottom", {"start": v(916.96, -895.45) * mm, "end": v(1016.96, -895.45) * mm});
            skLineSegment(sketch, "E211.top", {"start": v(916.96, -913.45) * mm, "end": v(1016.96, -913.45) * mm});
            skLineSegment(sketch, "E211.left", {"start": v(916.96, -895.45) * mm, "end": v(916.96, -913.45) * mm});
            skLineSegment(sketch, "E211.right", {"start": v(1016.96, -895.45) * mm, "end": v(1016.96, -913.45) * mm});
            skLineSegment(sketch, "E212.MirrorCS", {"start": v(1969.96, -913.45) * mm, "end": v(1869.96, -913.45) * mm});
            skLineSegment(sketch, "E213.MirrorCS", {"start": v(1969.96, -895.45) * mm, "end": v(1869.96, -895.45) * mm});
            skLineSegment(sketch, "E214.MirrorCS", {"start": v(1869.96, -895.45) * mm, "end": v(1869.96, -913.45) * mm});
            skLineSegment(sketch, "E215.MirrorCS", {"start": v(1502.96, -913.45) * mm, "end": v(1402.96, -913.45) * mm});
            skLineSegment(sketch, "E216.MirrorCS", {"start": v(1502.96, -895.45) * mm, "end": v(1502.96, -913.45) * mm});
            skLineSegment(sketch, "E217.MirrorCS", {"start": v(1502.96, -895.45) * mm, "end": v(1402.96, -895.45) * mm});
            skLineSegment(sketch, "E218.MirrorCS", {"start": v(1402.96, -895.45) * mm, "end": v(1402.96, -913.45) * mm});
            skLineSegment(sketch, "E219.bottom", {"start": v(449.96, -104.45) * mm, "end": v(467.96, -104.45) * mm});
            skLineSegment(sketch, "E219.top", {"start": v(449.96, -1984.45) * mm, "end": v(467.96, -1984.45) * mm});
            skLineSegment(sketch, "E219.right", {"start": v(467.96, -104.45) * mm, "end": v(467.96, -204.45) * mm});
            skLineSegment(sketch, "E220.bottom", {"start": v(1969.96, -1984.45) * mm, "end": v(1951.96, -1984.45) * mm});
            skLineSegment(sketch, "E220.top", {"start": v(1969.96, -104.45) * mm, "end": v(1951.96, -104.45) * mm});
            skLineSegment(sketch, "E220.left", {"start": v(1969.96, -1984.45) * mm, "end": v(1969.96, -104.45) * mm});
            skLineSegment(sketch, "E220.right", {"start": v(1951.96, -1984.45) * mm, "end": v(1951.96, -1884.45) * mm});
            skLineSegment(sketch, "E221.bottom", {"start": v(467.96, -955.45) * mm, "end": v(449.96, -955.45) * mm});
            skLineSegment(sketch, "E221.top", {"start": v(467.96, -853.45) * mm, "end": v(449.96, -853.45) * mm});
            skLineSegment(sketch, "E221.left", {"start": v(467.96, -955.45) * mm, "end": v(467.96, -853.45) * mm});
            skLineSegment(sketch, "E221.right", {"start": v(449.96, -955.45) * mm, "end": v(449.96, -853.45) * mm});
            skLineSegment(sketch, "E222.bottom", {"start": v(1951.96, -853.45) * mm, "end": v(1969.96, -853.45) * mm});
            skLineSegment(sketch, "E222.top", {"start": v(1951.96, -955.45) * mm, "end": v(1969.96, -955.45) * mm});
            skLineSegment(sketch, "E222.left", {"start": v(1951.96, -853.45) * mm, "end": v(1951.96, -955.45) * mm});
            skLineSegment(sketch, "E222.right", {"start": v(1969.96, -853.45) * mm, "end": v(1969.96, -955.45) * mm});
            skLineSegment(sketch, "E223.trimOffspring", {"start": v(467.96, -1884.45) * mm, "end": v(467.96, -1984.45) * mm});
            skLineSegment(sketch, "E224.trimOffspring", {"start": v(467.96, -853.45) * mm, "end": v(467.96, -955.45) * mm});
            skLineSegment(sketch, "E225.trimOffspring", {"start": v(1951.96, -955.45) * mm, "end": v(1951.96, -853.45) * mm});
            skLineSegment(sketch, "E226.trimOffspring", {"start": v(1951.96, -204.45) * mm, "end": v(1951.96, -104.45) * mm});
            skLineSegment(sketch, "E227", {"start": v(733.46, -895.45) * mm, "end": v(916.96, -895.45) * mm});
            skLineSegment(sketch, "E228", {"start": v(1016.96, -895.45) * mm, "end": v(1402.96, -895.45) * mm});
            skLineSegment(sketch, "E229", {"start": v(1502.96, -895.45) * mm, "end": v(1686.46, -895.45) * mm});
            skLineSegment(sketch, "E230.bottom", {"start": v(1016.96, -104.45) * mm, "end": v(1402.96, -104.45) * mm});
            skLineSegment(sketch, "E230.top", {"start": v(1016.96, -122.45) * mm, "end": v(1402.96, -122.45) * mm});
            skLineSegment(sketch, "E230.right", {"start": v(1402.96, -104.45) * mm, "end": v(1402.96, -122.45) * mm});
            skLineSegment(sketch, "E231.bottom", {"start": v(549.96, -913.45) * mm, "end": v(733.46, -913.45) * mm});
            skLineSegment(sketch, "E231.left", {"start": v(549.96, -913.45) * mm, "end": v(549.96, -895.45) * mm});
            skLineSegment(sketch, "E231.right", {"start": v(733.46, -913.45) * mm, "end": v(733.46, -895.45) * mm});
            skLineSegment(sketch, "E232.bottom", {"start": v(1869.96, -913.45) * mm, "end": v(1686.46, -913.45) * mm});
            skLineSegment(sketch, "E232.left", {"start": v(1869.96, -913.45) * mm, "end": v(1869.96, -895.45) * mm});
            skLineSegment(sketch, "E232.right", {"start": v(1686.46, -913.45) * mm, "end": v(1686.46, -895.45) * mm});
            skPoint(sketch, "E233.second.point", {"position": v(733.46, -899.45) * mm});
            skPoint(sketch, "E233.third.point", {"position": v(742.46, -895.45) * mm});
            skCircle(sketch, "E234", {"center": v(546.76, -897.84) * mm, "radius": 4 * mm});
            skPoint(sketch, "E234.second.point", {"position": v(543.55, -895.45) * mm});
            skPoint(sketch, "E234.third.point", {"position": v(549.96, -900.23) * mm});
            skLineSegment(sketch, "E235", {"start": v(549.96, -895.45) * mm, "end": v(541.4, -901.91) * mm, "construction": true});
            skArc(sketch, "E236", {"start": v(739.12, -895.45) * mm, "mid": v(733.46, -895.45) * mm, "end": v(733.46, -901.1) * mm});
            skLineSegment(sketch, "E237", {"start": v(733.46, -895.45) * mm, "end": v(736.3, -898.28) * mm});
            skCircle(sketch, "E238", {"center": v(465.14, -856.28) * mm, "radius": 4 * mm});
            skLineSegment(sketch, "E239", {"start": v(467.96, -853.45) * mm, "end": v(465.14, -856.28) * mm});
            skCircle(sketch, "E240", {"center": v(465.14, -201.62) * mm, "radius": 4 * mm});
            skLineSegment(sketch, "E241", {"start": v(467.96, -204.45) * mm, "end": v(465.14, -201.62) * mm});
            skCircle(sketch, "E242", {"center": v(547.14, -119.62) * mm, "radius": 4 * mm});
            skLineSegment(sketch, "E243", {"start": v(549.96, -122.45) * mm, "end": v(547.14, -119.62) * mm});
            skCircle(sketch, "E244", {"center": v(919.8, -119.62) * mm, "radius": 4 * mm});
            skLineSegment(sketch, "E245", {"start": v(916.96, -122.45) * mm, "end": v(919.8, -119.62) * mm});
            skCircle(sketch, "E246", {"center": v(1019.8, -201.62) * mm, "radius": 4 * mm});
            skLineSegment(sketch, "E247", {"start": v(1016.96, -204.45) * mm, "end": v(1019.8, -201.62) * mm});
            skCircle(sketch, "E248", {"center": v(1032.14, -201.62) * mm, "radius": 4 * mm});
            skLineSegment(sketch, "E249", {"start": v(1032.14, -201.62) * mm, "end": v(1034.96, -204.45) * mm});
            skCircle(sketch, "E250.MirrorC", {"center": v(1872.8, -119.62) * mm, "radius": 4 * mm});
            skCircle(sketch, "E251.MirrorC", {"center": v(1954.8, -201.62) * mm, "radius": 4 * mm});
            skCircle(sketch, "E252.MirrorC", {"center": v(1500.14, -119.62) * mm, "radius": 4 * mm});
            skCircle(sketch, "E253.MirrorC", {"center": v(1400.14, -201.62) * mm, "radius": 4 * mm});
            skCircle(sketch, "E254.MirrorC", {"center": v(1387.8, -201.62) * mm, "radius": 4 * mm});
            skCircle(sketch, "E255.MirrorC", {"center": v(1954.8, -856.28) * mm, "radius": 4 * mm});
            skCircle(sketch, "E256.MirrorC", {"center": v(1873.17, -897.84) * mm, "radius": 4 * mm});
            skArc(sketch, "E257.MirrorCS", {"start": v(1680.8, -895.45) * mm, "mid": v(1686.46, -895.45) * mm, "end": v(1686.46, -901.1) * mm});
            skCircle(sketch, "E258", {"center": v(1014.14, -910.62) * mm, "radius": 4 * mm});
            skLineSegment(sketch, "E259", {"start": v(1014.14, -910.62) * mm, "end": v(1016.96, -913.45) * mm});
            skCircle(sketch, "E260", {"center": v(919.8, -910.62) * mm, "radius": 4 * mm});
            skLineSegment(sketch, "E261", {"start": v(916.96, -913.45) * mm, "end": v(919.8, -910.62) * mm});
            skArc(sketch, "E262", {"start": v(727.8, -913.45) * mm, "mid": v(733.46, -913.45) * mm, "end": v(733.46, -907.8) * mm});
            skLineSegment(sketch, "E263", {"start": v(733.46, -913.45) * mm, "end": v(730.64, -910.62) * mm});
            skCircle(sketch, "E264", {"center": v(465.14, -952.62) * mm, "radius": 4 * mm});
            skLineSegment(sketch, "E265", {"start": v(467.96, -955.45) * mm, "end": v(465.14, -952.62) * mm});
            skCircle(sketch, "E266", {"center": v(465.14, -1887.28) * mm, "radius": 4 * mm});
            skLineSegment(sketch, "E267", {"start": v(467.96, -1884.45) * mm, "end": v(465.14, -1887.28) * mm});
            skCircle(sketch, "E268", {"center": v(547.14, -1969.28) * mm, "radius": 4 * mm});
            skLineSegment(sketch, "E269", {"start": v(549.96, -1966.45) * mm, "end": v(547.14, -1969.28) * mm});
            skCircle(sketch, "E270", {"center": v(919.8, -1969.28) * mm, "radius": 4 * mm});
            skLineSegment(sketch, "E271", {"start": v(916.96, -1966.45) * mm, "end": v(919.8, -1969.28) * mm});
            skCircle(sketch, "E272", {"center": v(1019.8, -1887.28) * mm, "radius": 4 * mm});
            skCircle(sketch, "E273", {"center": v(1032.14, -1887.28) * mm, "radius": 4 * mm});
            skLineSegment(sketch, "E274", {"start": v(1034.96, -1884.45) * mm, "end": v(1032.14, -1887.28) * mm});
            skLineSegment(sketch, "E275", {"start": v(1016.96, -1884.45) * mm, "end": v(1019.8, -1887.28) * mm});
            skCircle(sketch, "E276.MirrorC", {"center": v(1387.8, -1887.28) * mm, "radius": 4 * mm});
            skCircle(sketch, "E277.MirrorC", {"center": v(1400.14, -1887.28) * mm, "radius": 4 * mm});
            skCircle(sketch, "E278.MirrorC", {"center": v(1500.14, -1969.28) * mm, "radius": 4 * mm});
            skCircle(sketch, "E279.MirrorC", {"center": v(1872.8, -1969.28) * mm, "radius": 4 * mm});
            skCircle(sketch, "E280.MirrorC", {"center": v(1954.8, -1887.28) * mm, "radius": 4 * mm});
            skCircle(sketch, "E281.MirrorC", {"center": v(1954.8, -952.62) * mm, "radius": 4 * mm});
            skArc(sketch, "E282.MirrorC", {"start": v(1692.12, -913.45) * mm, "mid": v(1686.46, -913.45) * mm, "end": v(1686.46, -907.8) * mm});
            skCircle(sketch, "E283.MirrorC", {"center": v(1500.14, -910.62) * mm, "radius": 4 * mm});
            skCircle(sketch, "E284.MirrorC", {"center": v(1405.8, -910.62) * mm, "radius": 4 * mm});
            skSolve(sketch);
        }
        {
            var Q0;
            {var subQ54=sQuery(id+"F10.wireOp",EDGE,"E211.bottom");Q0=makeQuery(id+"F10.imprint","IMPRINT",FACE,{"disambiguationData":[TD([[makeQuery(id+"F10.imprint","IMPRINT",EDGE,{"derivedFrom":subQ54}),1.0]])]});}
            extrude(context, id + "F11", {"entities" : qUnion([Q0]), "depth" : (getVariable(context, 'Base')) * mm, "offsetDistance" : 25 * mm});
        }
        {
            var Q0;
            Q0=qCreatedBy(makeId("Top.planeOp"),FACE);
            var sketch = newSketch(context, id + "F12", { "sketchPlane" : qUnion([Q0])});
            skLineSegment(sketch, "E285.bottom", {"start": v(-1484, -691.72) * mm, "end": v(0, -691.72) * mm});
            skLineSegment(sketch, "E285.top", {"start": v(-1484, -1071.72) * mm, "end": v(-1035, -1071.72) * mm});
            skLineSegment(sketch, "E285.left", {"start": v(-1484, -691.72) * mm, "end": v(-1484, -1071.72) * mm});
            skLineSegment(sketch, "E285.right", {"start": v(0, -691.72) * mm, "end": v(0, -1071.72) * mm});
            skLineSegment(sketch, "E286.bottom", {"start": v(-1484, -691.72) * mm, "end": v(-1402, -691.72) * mm});
            skLineSegment(sketch, "E286.left", {"start": v(-1484, -691.72) * mm, "end": v(-1484, -704.72) * mm});
            skLineSegment(sketch, "E286.right", {"start": v(-1402, -691.72) * mm, "end": v(-1402, -704.72) * mm});
            skLineSegment(sketch, "E287", {"start": v(-742, -691.72) * mm, "end": v(-742, -708.72) * mm, "construction": true});
            skLineSegment(sketch, "E288.right", {"start": v(-1035, -691.72) * mm, "end": v(-1035, -704.72) * mm});
            skLineSegment(sketch, "E289.bottom", {"start": v(-1035, -1071.72) * mm, "end": v(-925.4, -1071.72) * mm});
            skLineSegment(sketch, "E289.left", {"start": v(-1035, -1071.72) * mm, "end": v(-1035, -1059.72) * mm});
            skLineSegment(sketch, "E290.left", {"start": v(-1484, -1071.72) * mm, "end": v(-1484, -1059.72) * mm});
            skLineSegment(sketch, "E290.right", {"start": v(-1402, -1071.72) * mm, "end": v(-1402, -1059.72) * mm});
            skLineSegment(sketch, "E291.bottom", {"start": v(-742, -708.72) * mm, "end": v(-892.4, -708.72) * mm});
            skLineSegment(sketch, "E291.top", {"start": v(-742, -1054.72) * mm, "end": v(-892.4, -1054.72) * mm});
            skLineSegment(sketch, "E291.right", {"start": v(-902.4, -718.72) * mm, "end": v(-902.4, -1044.72) * mm});
            skPoint(sketch, "E292.visualSharp", {"position": v(-902.4, -708.72) * mm});
            skArc(sketch, "E292.filletArc", {"start": v(-892.4, -708.72) * mm, "mid": v(-899.46, -711.65) * mm, "end": v(-902.4, -718.72) * mm});
            skPoint(sketch, "E293.visualSharp", {"position": v(-902.4, -1054.72) * mm});
            skArc(sketch, "E293.filletArc", {"start": v(-902.4, -1044.72) * mm, "mid": v(-899.46, -1051.8) * mm, "end": v(-892.4, -1054.72) * mm});
            skLineSegment(sketch, "E294.trimOffspring", {"start": v(-742, -1054.72) * mm, "end": v(-742, -1071.72) * mm, "construction": true});
            skLineSegment(sketch, "E295.0", {"start": v(-732.4, -1049.72) * mm, "end": v(-892.4, -1049.72) * mm});
            skLineSegment(sketch, "E295.1", {"start": v(-897.4, -718.72) * mm, "end": v(-897.4, -1044.72) * mm});
            skLineSegment(sketch, "E295.2", {"start": v(-732.4, -713.72) * mm, "end": v(-892.4, -713.72) * mm});
            skLineSegment(sketch, "E296", {"start": v(-1402, -704.72) * mm, "end": v(-1035, -704.72) * mm});
            skLineSegment(sketch, "E297", {"start": v(-1402, -1059.72) * mm, "end": v(-1035, -1059.72) * mm});
            skLineSegment(sketch, "E298.trimOffspring", {"start": v(-925.4, -1071.72) * mm, "end": v(0, -1071.72) * mm});
            skLineSegment(sketch, "E299.MirrorCS", {"start": v(-732.4, -713.72) * mm, "end": v(-591.6, -713.72) * mm});
            skLineSegment(sketch, "E300.MirrorCS", {"start": v(-742, -708.72) * mm, "end": v(-591.6, -708.72) * mm});
            skArc(sketch, "E301.MirrorCS", {"start": v(-591.6, -708.72) * mm, "mid": v(-584.54, -711.65) * mm, "end": v(-581.6, -718.72) * mm});
            skLineSegment(sketch, "E302.MirrorCS", {"start": v(-581.6, -718.72) * mm, "end": v(-581.6, -1044.72) * mm});
            skLineSegment(sketch, "E303.MirrorCS", {"start": v(-586.6, -718.72) * mm, "end": v(-586.6, -1044.72) * mm});
            skLineSegment(sketch, "E304.MirrorCS", {"start": v(-732.4, -1049.72) * mm, "end": v(-591.6, -1049.72) * mm});
            skArc(sketch, "E305.MirrorCS", {"start": v(-581.6, -1044.72) * mm, "mid": v(-584.54, -1051.8) * mm, "end": v(-591.6, -1054.72) * mm});
            skLineSegment(sketch, "E306.MirrorCS", {"start": v(-742, -1054.72) * mm, "end": v(-591.6, -1054.72) * mm});
            skLineSegment(sketch, "E307.MirrorCS", {"start": v(-449, -1071.72) * mm, "end": v(-449, -1059.72) * mm});
            skLineSegment(sketch, "E308.MirrorCS", {"start": v(-82, -1059.72) * mm, "end": v(-449, -1059.72) * mm});
            skLineSegment(sketch, "E309.MirrorCS", {"start": v(-82, -1071.72) * mm, "end": v(-82, -1059.72) * mm});
            skLineSegment(sketch, "E310.MirrorCS", {"start": v(-82, -691.72) * mm, "end": v(-82, -704.72) * mm});
            skLineSegment(sketch, "E311.MirrorCS", {"start": v(-82, -704.72) * mm, "end": v(-449, -704.72) * mm});
            skLineSegment(sketch, "E312.MirrorCS", {"start": v(-449, -691.72) * mm, "end": v(-449, -704.72) * mm});
            skPoint(sketch, "E313.visualSharp", {"position": v(-897.4, -713.72) * mm});
            skArc(sketch, "E313.filletArc", {"start": v(-892.4, -713.72) * mm, "mid": v(-895.93, -715.19) * mm, "end": v(-897.4, -718.72) * mm});
            skPoint(sketch, "E314.visualSharp", {"position": v(-897.4, -1049.72) * mm});
            skPoint(sketch, "E315.visualSharp", {"position": v(-586.6, -713.72) * mm});
            skArc(sketch, "E315.filletArc", {"start": v(-586.6, -718.72) * mm, "mid": v(-588.07, -715.19) * mm, "end": v(-591.6, -713.72) * mm});
            skPoint(sketch, "E316.visualSharp", {"position": v(-586.6, -1049.72) * mm});
            skArc(sketch, "E316.filletArc", {"start": v(-591.6, -1049.72) * mm, "mid": v(-588.07, -1048.26) * mm, "end": v(-586.6, -1044.72) * mm});
            skPoint(sketch, "E317.orphan", {"position": v(-1402, -704.72) * mm});
            skPoint(sketch, "E318.second.point", {"position": v(-1035, -700.72) * mm});
            skPoint(sketch, "E318.third.point", {"position": v(-1029, -704.72) * mm});
            skCircle(sketch, "E319", {"center": v(-447, -702.72) * mm, "radius": 2.83 * mm});
            skPoint(sketch, "E319.second.point", {"position": v(-449, -700.72) * mm});
            skPoint(sketch, "E319.third.point", {"position": v(-445, -704.72) * mm});
            skPoint(sketch, "E320.orphan", {"position": v(-449, -696.72) * mm});
            skCircle(sketch, "E321", {"center": v(-84, -702.72) * mm, "radius": 2.83 * mm});
            skPoint(sketch, "E321.second.point", {"position": v(-82, -700.72) * mm});
            skPoint(sketch, "E321.third.point", {"position": v(-86, -704.72) * mm});
            skPoint(sketch, "E322.orphan", {"position": v(-1035, -696.72) * mm});
            skPoint(sketch, "E323.second.point", {"position": v(-1402, -1063.72) * mm});
            skPoint(sketch, "E323.third.point", {"position": v(-1378, -1059.72) * mm});
            skPoint(sketch, "E324.orphan", {"position": v(-1402, -1067.72) * mm});
            skPoint(sketch, "E325.second.point", {"position": v(-1029, -1059.72) * mm});
            skPoint(sketch, "E325.third.point", {"position": v(-1035, -1063.72) * mm});
            skCircle(sketch, "E326", {"center": v(-447, -1061.72) * mm, "radius": 2.83 * mm});
            skPoint(sketch, "E326.second.point", {"position": v(-449, -1063.72) * mm});
            skPoint(sketch, "E326.third.point", {"position": v(-445, -1059.72) * mm});
            skPoint(sketch, "E327.orphan", {"position": v(-82, -1067.72) * mm});
            skCircle(sketch, "E328", {"center": v(-84, -1061.72) * mm, "radius": 2.83 * mm});
            skPoint(sketch, "E328.second.point", {"position": v(-82, -1063.72) * mm});
            skPoint(sketch, "E328.third.point", {"position": v(-86, -1059.72) * mm});
            skCircle(sketch, "E329", {"center": v(-1399.17, -701.9) * mm, "radius": 4 * mm});
            skLineSegment(sketch, "E330", {"start": v(-1402, -704.72) * mm, "end": v(-1399.17, -701.9) * mm});
            skCircle(sketch, "E331", {"center": v(-1037.83, -701.9) * mm, "radius": 4 * mm});
            skLineSegment(sketch, "E332", {"start": v(-1035, -704.72) * mm, "end": v(-1037.83, -701.9) * mm});
            skCircle(sketch, "E333", {"center": v(-1037.83, -1062.55) * mm, "radius": 4 * mm});
            skLineSegment(sketch, "E334", {"start": v(-1035, -1059.72) * mm, "end": v(-1037.83, -1062.55) * mm});
            skCircle(sketch, "E335", {"center": v(-1399.17, -1062.55) * mm, "radius": 4 * mm});
            skLineSegment(sketch, "E336", {"start": v(-1402, -1059.72) * mm, "end": v(-1399.17, -1062.55) * mm});
            skCircle(sketch, "E337.MirrorC", {"center": v(-446.17, -701.9) * mm, "radius": 4 * mm});
            skCircle(sketch, "E338.MirrorC", {"center": v(-84.83, -701.9) * mm, "radius": 4 * mm});
            skCircle(sketch, "E339.MirrorC", {"center": v(-84.83, -1062.55) * mm, "radius": 4 * mm});
            skCircle(sketch, "E340.MirrorC", {"center": v(-446.17, -1062.55) * mm, "radius": 4 * mm});
            skPoint(sketch, "E341.orphan", {"position": v(-751.6, -1049.72) * mm});
            skArc(sketch, "E342.filletArc", {"start": v(-897.4, -1044.72) * mm, "mid": v(-895.93, -1048.26) * mm, "end": v(-892.4, -1049.72) * mm});
            skSolve(sketch);
        }
        {
            var Q0;
            {var subQ44=sQuery(id+"F2.wireOp",EDGE,"E43");Q0=makeQuery(id+"F2.imprint","IMPRINT",FACE,{"disambiguationData":[TD([[makeQuery(id+"F2.imprint","IMPRINT",EDGE,{"derivedFrom":subQ44}),-1.0]])]});}
            extrude(context, id + "F13", {"entities" : qUnion([Q0]), "depth" : (getVariable(context, 'Base')) * mm, "offsetDistance" : 25 * mm});
        }
        {
            var Q0;
            {var subQ51=sQuery(id+"F12.wireOp",EDGE,"E285.right");Q0=makeQuery(id+"F12.imprint","IMPRINT",FACE,{"disambiguationData":[TD([[makeQuery(id+"F12.imprint","IMPRINT",EDGE,{"derivedFrom":subQ51}),-1.0]])]});}
            var Q1;
            Q1=makeQuery(id+"F12.imprint","IMPRINT",FACE,{"disambiguationData":[TD([[makeQuery(id+"F12.imprint","IMPRINT",EDGE,{"derivedFrom":sQuery(id+"F12.wireOp",EDGE,"E295.0")}),-1.0]])]});
            extrude(context, id + "F14", {"entities" : qUnion([Q0, Q1]), "oppositeDirection" : true, "depth" : (getVariable(context, 'thickness')) * mm, "offsetDistance" : 25 * mm});
        }
        {
            var Q0;
            {var subQ17=sQuery(id+"F10.wireOp",EDGE,"E228");Q0=makeQuery(id+"F10.imprint","IMPRINT",FACE,{"disambiguationData":[TD([[makeQuery(id+"F10.imprint","IMPRINT",EDGE,{"derivedFrom":subQ17}),-1.0]])]});}
            extrude(context, id + "F15", {"entities" : qUnion([Q0]), "depth" : 12 * mm, "offsetDistance" : 25 * mm});
        }
    });
